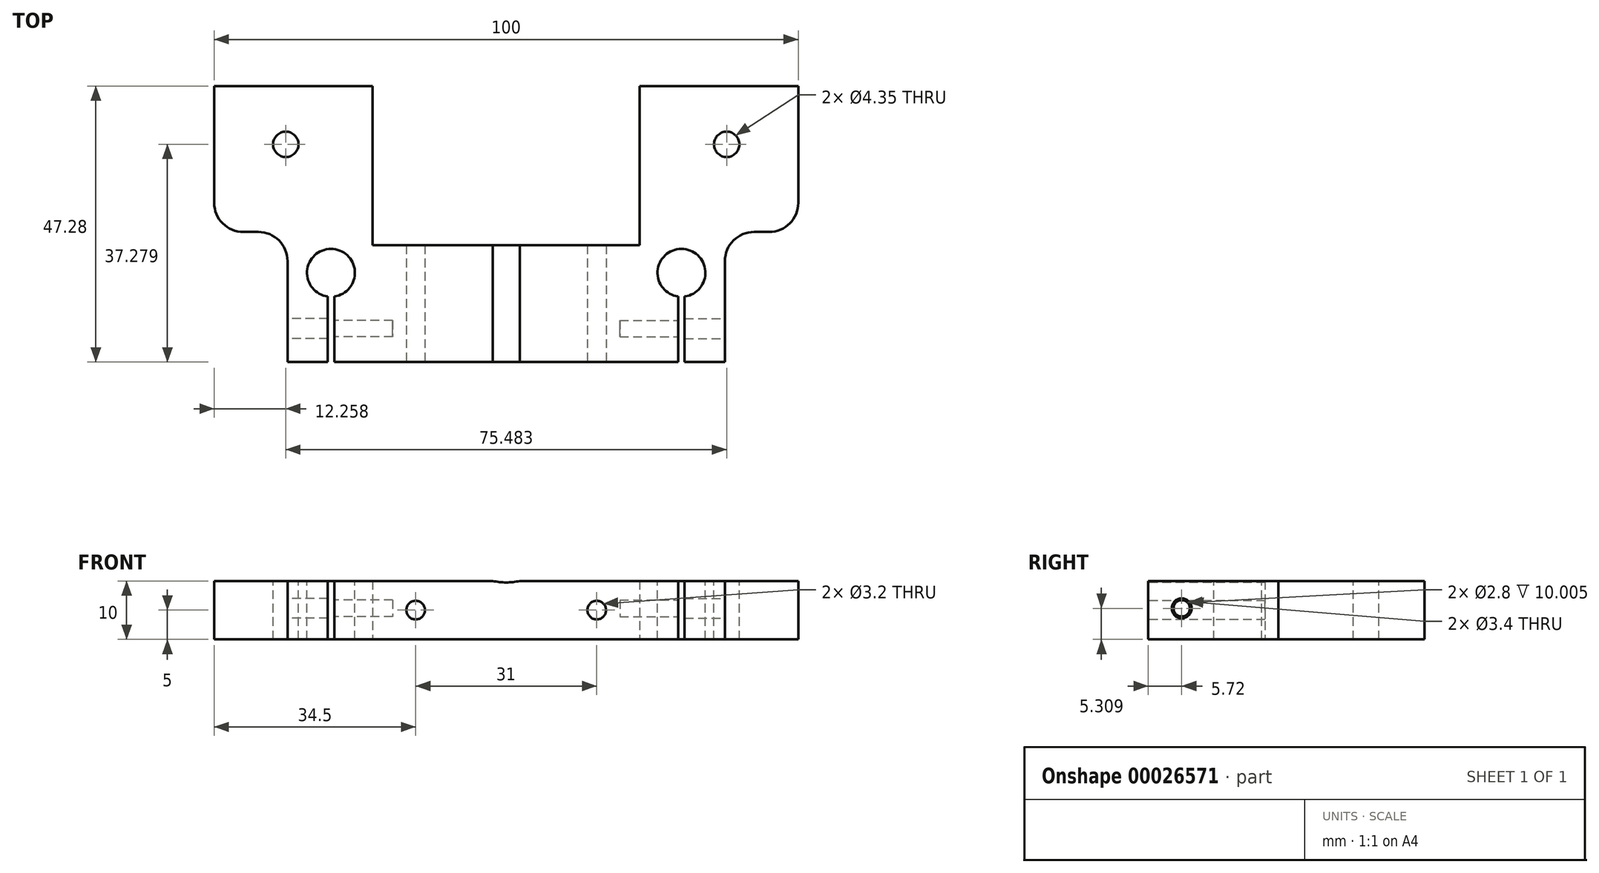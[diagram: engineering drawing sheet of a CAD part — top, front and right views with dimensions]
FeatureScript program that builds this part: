
annotation { "Feature Type Name" : "Feature", "Feature Type Description" : "" }
export const myFeature = defineFeature(function(context is Context, id is Id, definition is map)
    precondition{}
    {
        {
            var Q0;
            Q0=qCreatedBy(makeId("Top.planeOp"),FACE);
            var sketch = newSketch(context, id + "F0", { "sketchPlane" : qUnion([Q0])});
            skLineSegment(sketch, "E0", {"start": v(0, -13.82) * mm, "end": v(-37.44, -13.82) * mm});
            skLineSegment(sketch, "E1", {"start": v(-37.44, -13.82) * mm, "end": v(-37.44, 8.46) * mm});
            skLineSegment(sketch, "E2", {"start": v(-37.44, 8.46) * mm, "end": v(-50, 8.46) * mm});
            skLineSegment(sketch, "E3", {"start": v(-50, 8.46) * mm, "end": v(-50, 33.46) * mm});
            skLineSegment(sketch, "E4", {"start": v(-50, 33.46) * mm, "end": v(-22.87, 33.46) * mm});
            skLineSegment(sketch, "E5", {"start": v(-22.87, 33.46) * mm, "end": v(-22.87, 6.18) * mm});
            skLineSegment(sketch, "E6", {"start": v(-22.87, 6.18) * mm, "end": v(0, 6.18) * mm});
            skLineSegment(sketch, "E7", {"start": v(0, 6.18) * mm, "end": v(0, -13.82) * mm});
            skSolve(sketch);
        }
        {
            var Q0;
            Q0=qSketchRegion(id+"F0",true);
            extrude(context, id + "F1", {"entities" : qUnion([Q0]), "depth" : 10 * mm});
        }
        {
            var Q0;
            Q0=makeQuery(id+"F1.opExtrude","SWEPT_FACE",FACE,{"disambiguationData":[OSD([sQuery(id+"F0.wireOp",EDGE,"E0")])]});
            var sketch = newSketch(context, id + "F2", { "sketchPlane" : qUnion([Q0])});
            skLineSegment(sketch, "E8", {"start": v(0, 5) * mm, "end": v(0, 5) * mm});
            skCircle(sketch, "E9", {"center": v(-15.5, 5) * mm, "radius": 1.6 * mm});
            skCircle(sketch, "E10", {"center": v(0, 20.5) * mm, "radius": 10.75 * mm});
            skSolve(sketch);
        }
        {
            var Q0;
            Q0=qSketchRegion(id+"F2",true);
            extrude(context, id + "F3", {"entities" : qUnion([Q0]), "operationType" : NewBodyOperationType.REMOVE, "endBound" : BoundingType.THROUGH_ALL, "oppositeDirection" : true, "depth" : 25 * mm});
        }
        {
            var Q0;
            {var subQ0=makeQuery(id+"F1.opExtrude","CAP_FACE",FACE,{"disambiguationData":[OSD([sQuery(id+"F0.wireOp",EDGE,"E0"),sQuery(id+"F0.wireOp",EDGE,"fd64a43a-5635-4f94-a977-4dd36923accb"),sQuery(id+"F0.wireOp",EDGE,"1334f7d4-4c90-4769-8fa3-fe5f576fb005"),sQuery(id+"F0.wireOp",EDGE,"E1"),sQuery(id+"F0.wireOp",EDGE,"E2"),sQuery(id+"F0.wireOp",EDGE,"E3"),sQuery(id+"F0.wireOp",EDGE,"E4"),sQuery(id+"F0.wireOp",EDGE,"E5"),sQuery(id+"F0.wireOp",EDGE,"E6"),sQuery(id+"F0.wireOp",EDGE,"E7")])],"isStart":false});Q0=makeQuery(id+"F11.boolean.opBoolean","MERGE",FACE,{"derivedFrom":[subQ0,makeQuery(id+"F11.opPattern","COPY",FACE,{"derivedFrom":subQ0,"instanceName":"1"})]});}
            var sketch = newSketch(context, id + "F4", { "sketchPlane" : qUnion([Q0])});
            skCircle(sketch, "E11", {"center": v(-30, 1.46) * mm, "radius": 4.1 * mm});
            skCircle(sketch, "E12", {"center": v(-37.74, 23.46) * mm, "radius": 2.17 * mm});
            skLineSegment(sketch, "E13", {"start": v(-30, 1.46) * mm, "end": v(-30, -13.82) * mm, "construction": true});
            skLineSegment(sketch, "E14.bottom", {"start": v(-30.55, -1.63) * mm, "end": v(-29.45, -1.63) * mm});
            skLineSegment(sketch, "E14.top", {"start": v(-30.55, -14.74) * mm, "end": v(-29.45, -14.74) * mm});
            skLineSegment(sketch, "E14.left", {"start": v(-30.55, -1.63) * mm, "end": v(-30.55, -14.74) * mm});
            skLineSegment(sketch, "E14.right", {"start": v(-29.45, -1.63) * mm, "end": v(-29.45, -14.74) * mm});
            skPoint(sketch, "E15", {"position": v(-30, -1.63) * mm});
            skSolve(sketch);
        }
        {
            var Q0;
            Q0=qSketchRegion(id+"F4",true);
            var Q1;
            {var subQ3=sQuery(id+"F4.wireOp",EDGE,"E14.bottom");Q1=makeQuery(id+"F4.imprint","IMPRINT",FACE,{"disambiguationData":[TD([[makeQuery(id+"F4.imprint","IMPRINT",EDGE,{"derivedFrom":subQ3}),-1.0]])]});}
            extrude(context, id + "F5", {"entities" : qUnion([Q0, Q1]), "operationType" : NewBodyOperationType.REMOVE, "endBound" : BoundingType.THROUGH_ALL, "oppositeDirection" : true, "depth" : 25 * mm});
        }
        {
            var Q0;
            Q0=makeQuery(id+"F1.opExtrude","SWEPT_EDGE",EDGE,{"disambiguationData":[OSD([sQuery(id+"F0.wireOp",EDGE,"E2"),sQuery(id+"F0.wireOp",EDGE,"E3")])]});
            fillet(context, id + "F6", {"entities" : qUnion([Q0]), "radius" : 5 * mm, "tangentPropagation" : true, "allowEdgeOverflow" : false});
        }
        {
            var Q0;
            Q0=makeQuery(id+"F1.opExtrude","SWEPT_EDGE",EDGE,{"disambiguationData":[OSD([sQuery(id+"F0.wireOp",EDGE,"E1"),sQuery(id+"F0.wireOp",EDGE,"E2")])]});
            fillet(context, id + "F7", {"entities" : qUnion([Q0]), "radius" : 5 * mm, "tangentPropagation" : true, "allowEdgeOverflow" : false});
        }
        {
            var Q0;
            Q0=makeQuery(id+"F1.opExtrude","SWEPT_FACE",FACE,{"disambiguationData":[OSD([sQuery(id+"F0.wireOp",EDGE,"E1")])]});
            var sketch = newSketch(context, id + "F8", { "sketchPlane" : qUnion([Q0])});
            skCircle(sketch, "E16", {"center": v(8.1, 5.3) * mm, "radius": 1.7 * mm});
            skCircle(sketch, "E17", {"center": v(8.1, 5.3) * mm, "radius": 1.4 * mm});
            skSolve(sketch);
        }
        {
            var Q0;
            Q0=makeQuery(id+"F8.imprint","IMPRINT",FACE,{"disambiguationData":[TD([[makeQuery(id+"F8.imprint","IMPRINT",EDGE,{"derivedFrom":sQuery(id+"F8.wireOp",EDGE,"E17")}),1.0]])]});
            extrude(context, id + "F9", {"entities" : qUnion([Q0]), "operationType" : NewBodyOperationType.REMOVE, "oppositeDirection" : true, "depth" : 18 * mm});
        }
        {
            var Q0;
            Q0=makeQuery(id+"F8.imprint","IMPRINT",FACE,{"disambiguationData":[TD([[makeQuery(id+"F8.imprint","IMPRINT",EDGE,{"derivedFrom":sQuery(id+"F8.wireOp",EDGE,"E17")}),1.0]])]});
            var Q1;
            Q1=makeQuery(id+"F8.imprint","IMPRINT",FACE,{"disambiguationData":[TD([[makeQuery(id+"F8.imprint","IMPRINT",EDGE,{"derivedFrom":sQuery(id+"F8.wireOp",EDGE,"E16")}),1.0]])]});
            extrude(context, id + "F10", {"entities" : qUnion([Q0, Q1]), "operationType" : NewBodyOperationType.REMOVE, "endBound" : BoundingType.UP_TO_NEXT, "oppositeDirection" : true, "depth" : 25 * mm});
        }
        {
            var Q0;
            Q0=makeQuery(id+"F1.opExtrude","SWEPT_BODY",BODY,{"disambiguationData":[OSD([sQuery(id+"F0.wireOp",EDGE,"E0"),sQuery(id+"F0.wireOp",EDGE,"fd64a43a-5635-4f94-a977-4dd36923accb"),sQuery(id+"F0.wireOp",EDGE,"1334f7d4-4c90-4769-8fa3-fe5f576fb005"),sQuery(id+"F0.wireOp",EDGE,"E1"),sQuery(id+"F0.wireOp",EDGE,"E2"),sQuery(id+"F0.wireOp",EDGE,"E3"),sQuery(id+"F0.wireOp",EDGE,"E4"),sQuery(id+"F0.wireOp",EDGE,"E5"),sQuery(id+"F0.wireOp",EDGE,"E6"),sQuery(id+"F0.wireOp",EDGE,"E7")])]});
            var Q1;
            Q1=qCreatedBy(makeId("Right.planeOp"),FACE);
            mirror(context, id + "F11", {"operationType" : NewBodyOperationType.ADD, "entities" : qUnion([Q0]), "mirrorPlane" : qUnion([Q1])});
        }
    });
